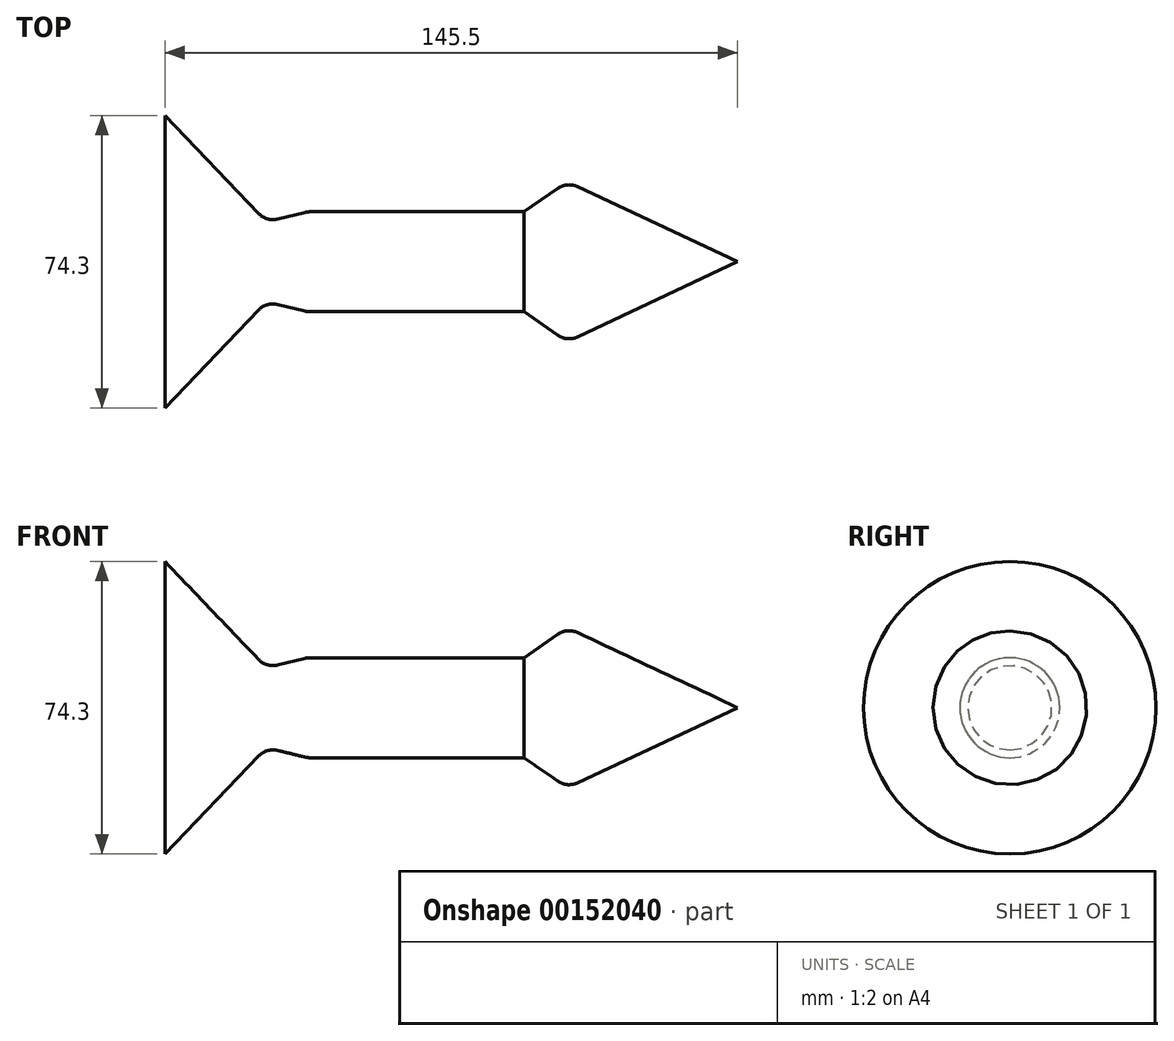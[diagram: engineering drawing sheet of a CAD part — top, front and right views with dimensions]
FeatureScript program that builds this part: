
annotation { "Feature Type Name" : "Feature", "Feature Type Description" : "" }
export const myFeature = defineFeature(function(context is Context, id is Id, definition is map)
    precondition{}
    {
        {
            var Q0;
            Q0=qCreatedBy(makeId("Top.planeOp"),FACE);
            var sketch = newSketch(context, id + "F0", { "sketchPlane" : qUnion([Q0])});
            skLineSegment(sketch, "E0", {"start": v(-66.76, 37.15) * mm, "end": v(-40.96, 10.16) * mm});
            skLineSegment(sketch, "E1", {"start": v(-40.96, 10.16) * mm, "end": v(-30.55, 12.7) * mm});
            skLineSegment(sketch, "E2", {"start": v(-30.55, 12.7) * mm, "end": v(24.48, 12.7) * mm});
            skLineSegment(sketch, "E3", {"start": v(24.48, 12.7) * mm, "end": v(35.42, 20.32) * mm});
            skLineSegment(sketch, "E4", {"start": v(35.42, 20.32) * mm, "end": v(78.74, 0) * mm});
            skLineSegment(sketch, "E5", {"start": v(78.74, 0) * mm, "end": v(-66.76, 0) * mm});
            skLineSegment(sketch, "E6", {"start": v(-66.76, 0) * mm, "end": v(-66.76, 37.15) * mm});
            skSolve(sketch);
        }
        {
            var Q0;
            Q0=makeQuery(id+"F0.imprint","IMPRINT",FACE,{"disambiguationData":[TD([[makeQuery(id+"F0.imprint","IMPRINT",EDGE,{"derivedFrom":sQuery(id+"F0.wireOp",EDGE,"E0")}),-1.0]])]});
            var Q1;
            Q1=sQuery(id+"F0.wireOp",EDGE,"E5");
            revolve(context, id + "F1", {"surfaceOperationType" : NewSurfaceOperationType.NEW, "entities" : qUnion([Q0]), "axis" : qUnion([Q1]), "revolveType" : RevolveType.FULL});
        }
        {
            var Q0;
            Q0=makeQuery(id+"F1.opRevolve","SWEPT_EDGE",EDGE,{"disambiguationData":[OSD([sQuery(id+"F0.wireOp",EDGE,"E0"),sQuery(id+"F0.wireOp",EDGE,"E1")])]});
            var Q1;
            Q1=makeQuery(id+"F1.opRevolve","SWEPT_EDGE",EDGE,{"disambiguationData":[OSD([sQuery(id+"F0.wireOp",EDGE,"E1"),sQuery(id+"F0.wireOp",EDGE,"E2")])]});
            var Q2;
            Q2=makeQuery(id+"F1.opRevolve","SWEPT_EDGE",EDGE,{"disambiguationData":[OSD([sQuery(id+"F0.wireOp",EDGE,"E3"),sQuery(id+"F0.wireOp",EDGE,"E4")])]});
            fillet(context, id + "F2", {"entities" : qUnion([Q0, Q1, Q2]), "radius" : 5.08 * mm, "tangentPropagation" : true, "allowEdgeOverflow" : false});
        }
    });
